# Revit family: Faucet-Lavatory-KOHLER-Taut-K-74026X_1
name_source: partatom
category: Plumbing Fixtures
units: mm (PartAtom-declared; Revit-internal decimal feet)

## family parameters
Cut with Voids When Loaded = No
Host = Face
OmniClass Number = 23.31.11.00
OmniClass Title = Faucets
Part Type = Normal
Room Calculation Point = No
Round Connector Dimension = Use Diameter
Shared = No

## types (2) — shared parameters
ADA Compliant = No
Assembly Code = D2010
CW Connection = Yes
Cold Water Inlet = Cold Water Inlet
Date Modified = 03/24/2023
Default Elevation = 36"
Description = Single Control Tall Lavatory Faucet With Drain
Drain Included = Yes
Flow Rate = 2 GPM
HW Connection = Yes
Handle Clearance = 3 7/16"
Height = 10 3/4"
Hot Water Inlet = Hot Water Inlet
Length = 4 3/4"
Manufacturer = Kohler Co.
Master Format 2014 = 22 41 39
Master Format 2014 Name = Residential Faucets, Supplies, and Trim
Material = Premium Metal Construction
Pressure = 0.00 psi
Product Documentation Link = https://resources.kohler.com
Product Name = Taut
Spout Reach = 4 3/4"
URL = https://www.kohlerasiapacific.com
Vent Connection = No
Waste Connection = No
Waste Water Outlet = Waste Water Outlet
WaterSense Certified = No
Width = 1 7/8"

## per-type parameters (varying)
| type | Finish | Model | Product Page URL | Type |
| CP-Polished Chrome | Kohler-Metal-CP-Polished_Chrome | K-74026X-4A-CP | https://www.kohlerasiapacific.com | 1 |
| NA-Stainless | Kohler-Metal-NA-Stainless | K-74026X-4A-NA |  | 2 |

## geometry (parser evidence)
native form markers: Sweep x5
no freeform markers — native parametric forms only
